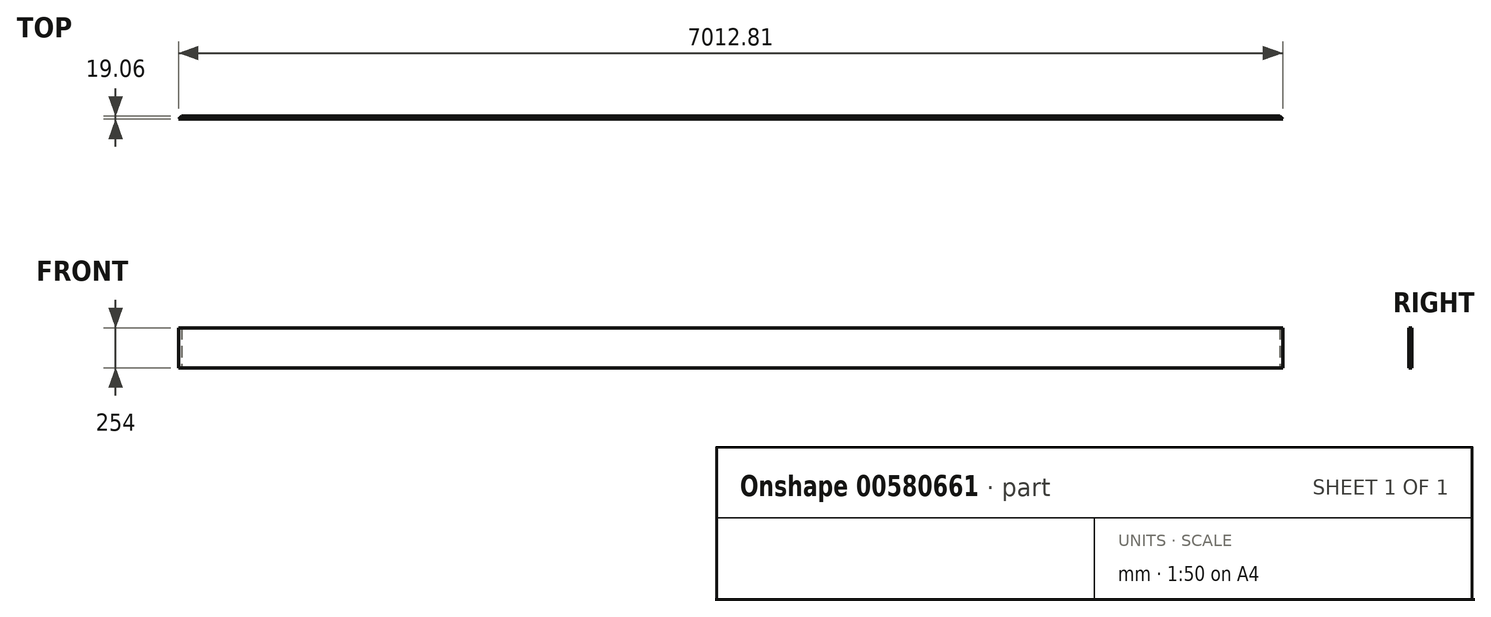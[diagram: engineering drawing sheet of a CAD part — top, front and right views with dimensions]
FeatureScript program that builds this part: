
annotation { "Feature Type Name" : "Feature", "Feature Type Description" : "" }
export const myFeature = defineFeature(function(context is Context, id is Id, definition is map)
    precondition{}
    {
        {
            var Q0;
            Q0=qCreatedBy(makeId("Top.planeOp"),FACE);
            var sketch = newSketch(context, id + "F0", { "sketchPlane" : qUnion([Q0])});
            skLineSegment(sketch, "E0.bottom", {"start": v(3320.29, -9.53) * mm, "end": v(-3692.52, -9.53) * mm});
            skLineSegment(sketch, "E0.top", {"start": v(3301.24, 9.52) * mm, "end": v(-3673.47, 9.52) * mm});
            skPoint(sketch, "E0.middle", {"position": v(0, 0) * mm});
            skLineSegment(sketch, "E1", {"start": v(-3692.52, -9.53) * mm, "end": v(-3673.47, 9.52) * mm});
            skPoint(sketch, "E2.orphan", {"position": v(-3320.29, 9.52) * mm});
            skLineSegment(sketch, "E3", {"start": v(3320.29, -9.53) * mm, "end": v(3301.24, 9.53) * mm});
            skPoint(sketch, "E0.left.end.orphan", {"position": v(3692.52, 9.53) * mm});
            skSolve(sketch);
        }
        {
            var Q0;
            Q0=makeQuery(id+"F0.imprint","IMPRINT",FACE,{"disambiguationData":[TD([[makeQuery(id+"F0.imprint","IMPRINT",EDGE,{"derivedFrom":sQuery(id+"F0.wireOp",EDGE,"E0.bottom")}),-1.0]])]});
            extrude(context, id + "F1", {"entities" : qUnion([Q0]), "depth" : 254 * mm, "offsetDistance" : 25.4 * mm});
        }
    });
